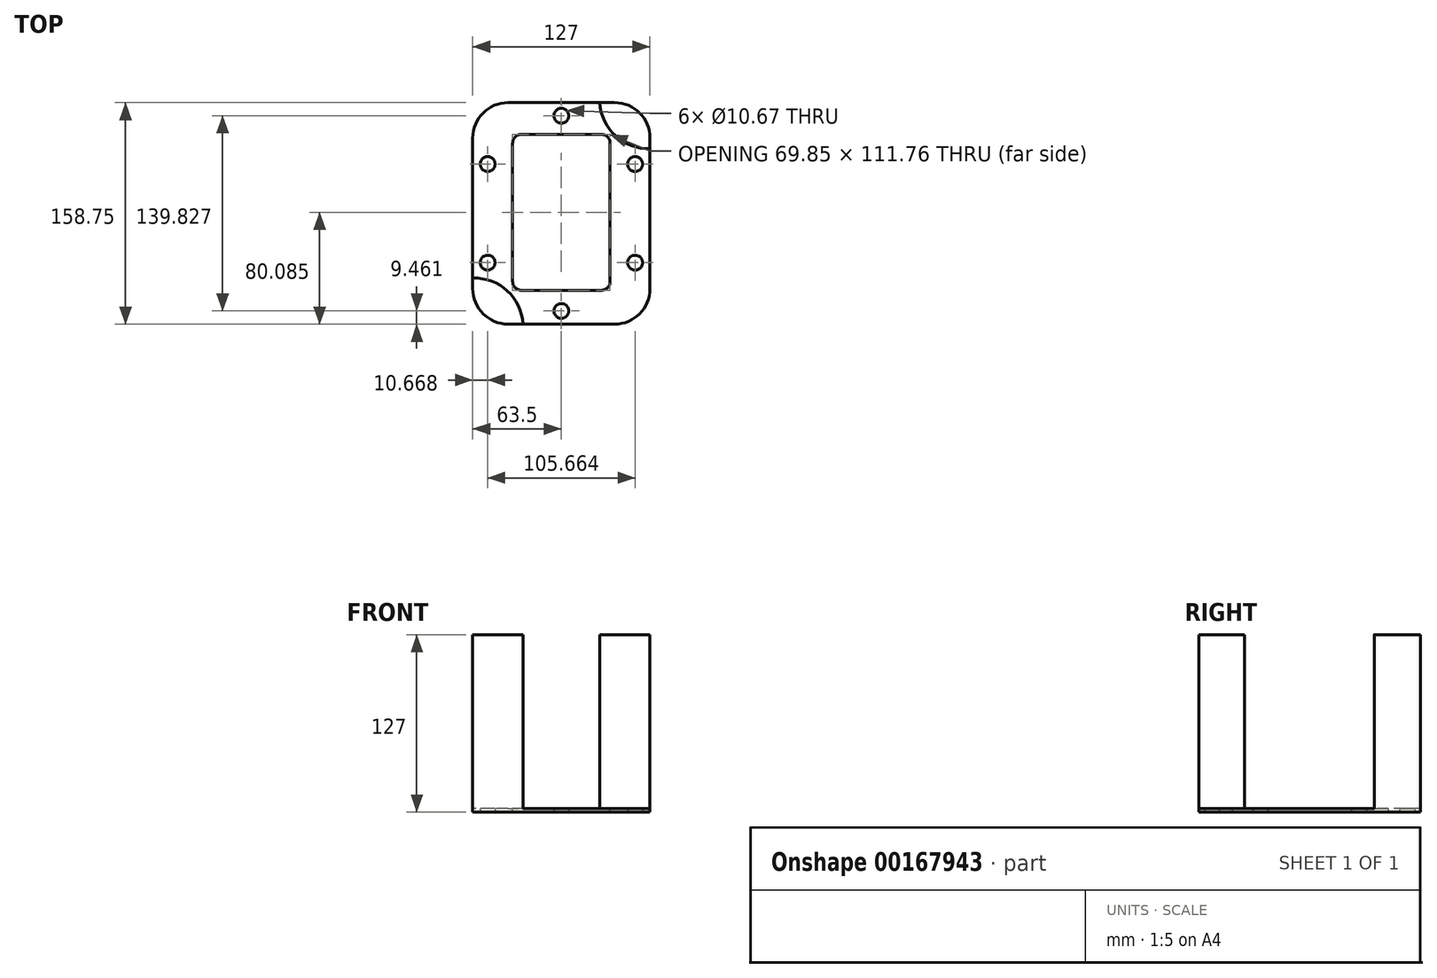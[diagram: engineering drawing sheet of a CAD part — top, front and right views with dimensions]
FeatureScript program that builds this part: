
annotation { "Feature Type Name" : "Feature", "Feature Type Description" : "" }
export const myFeature = defineFeature(function(context is Context, id is Id, definition is map)
    precondition{}
    {
        {
            var Q0;
            Q0=qCreatedBy(makeId("Top.planeOp"),FACE);
            var sketch = newSketch(context, id + "F0", { "sketchPlane" : qUnion([Q0])});
            skLineSegment(sketch, "E0.bottom", {"start": v(25.4, 0) * mm, "end": v(101.6, 0) * mm});
            skLineSegment(sketch, "E0.top", {"start": v(25.4, 158.75) * mm, "end": v(101.6, 158.75) * mm});
            skLineSegment(sketch, "E0.left", {"start": v(0, 25.4) * mm, "end": v(0, 133.35) * mm});
            skLineSegment(sketch, "E0.right", {"start": v(127, 25.4) * mm, "end": v(127, 133.35) * mm});
            skLineSegment(sketch, "E1", {"start": v(63.5, 0) * mm, "end": v(63.5, 158.75) * mm});
            skLineSegment(sketch, "E2", {"start": v(0, 79.38) * mm, "end": v(127, 79.38) * mm});
            skLineSegment(sketch, "E3", {"start": v(116.33, 79.38) * mm, "end": v(116.33, 114.68) * mm});
            skCircle(sketch, "E4", {"center": v(116.33, 114.68) * mm, "radius": 5.33 * mm});
            skCircle(sketch, "E5.MirrorC", {"center": v(10.67, 114.68) * mm, "radius": 5.33 * mm});
            skCircle(sketch, "E6.MirrorC", {"center": v(10.67, 44.07) * mm, "radius": 5.33 * mm});
            skCircle(sketch, "E7.MirrorC", {"center": v(116.33, 44.07) * mm, "radius": 5.33 * mm});
            skCircle(sketch, "E8", {"center": v(63.5, 149.29) * mm, "radius": 5.33 * mm});
            skCircle(sketch, "E9.MirrorC", {"center": v(63.5, 9.46) * mm, "radius": 5.33 * mm});
            skPoint(sketch, "E10.visualSharp", {"position": v(0, 158.75) * mm});
            skArc(sketch, "E10.filletArc", {"start": v(25.4, 158.75) * mm, "mid": v(7.44, 151.31) * mm, "end": v(0, 133.35) * mm});
            skPoint(sketch, "E11.visualSharp", {"position": v(0, 0) * mm});
            skArc(sketch, "E11.filletArc", {"start": v(0, 25.4) * mm, "mid": v(7.44, 7.44) * mm, "end": v(25.4, 0) * mm});
            skPoint(sketch, "E12.visualSharp", {"position": v(127, 0) * mm});
            skArc(sketch, "E12.filletArc", {"start": v(101.6, 0) * mm, "mid": v(119.56, 7.44) * mm, "end": v(127, 25.4) * mm});
            skPoint(sketch, "E13.visualSharp", {"position": v(127, 158.75) * mm});
            skArc(sketch, "E13.filletArc", {"start": v(127, 133.35) * mm, "mid": v(119.56, 151.31) * mm, "end": v(101.6, 158.75) * mm});
            skLineSegment(sketch, "E14.bottom", {"start": v(95.25, 135.26) * mm, "end": v(31.75, 135.26) * mm});
            skLineSegment(sketch, "E14.top", {"start": v(95.25, 23.5) * mm, "end": v(31.75, 23.5) * mm});
            skLineSegment(sketch, "E14.left", {"start": v(101.6, 128.9) * mm, "end": v(101.6, 29.84) * mm});
            skLineSegment(sketch, "E14.right", {"start": v(25.4, 128.9) * mm, "end": v(25.4, 29.84) * mm});
            skPoint(sketch, "E14.middle", {"position": v(63.5, 79.38) * mm});
            skPoint(sketch, "E15.visualSharp", {"position": v(25.4, 135.26) * mm});
            skArc(sketch, "E15.filletArc", {"start": v(31.75, 135.26) * mm, "mid": v(27.26, 133.4) * mm, "end": v(25.4, 128.9) * mm});
            skPoint(sketch, "E16.visualSharp", {"position": v(101.6, 135.26) * mm});
            skArc(sketch, "E16.filletArc", {"start": v(101.6, 128.9) * mm, "mid": v(99.74, 133.4) * mm, "end": v(95.25, 135.26) * mm});
            skPoint(sketch, "E17.visualSharp", {"position": v(101.6, 23.5) * mm});
            skArc(sketch, "E17.filletArc", {"start": v(95.25, 23.5) * mm, "mid": v(99.74, 25.35) * mm, "end": v(101.6, 29.84) * mm});
            skPoint(sketch, "E18.visualSharp", {"position": v(25.4, 23.5) * mm});
            skArc(sketch, "E18.filletArc", {"start": v(25.4, 29.84) * mm, "mid": v(27.26, 25.35) * mm, "end": v(31.75, 23.5) * mm});
            skSolve(sketch);
        }
        {
            var Q0;
            Q0 = qSketchRegion(id + "F0", true);
            var Q1;
            {var subQ0=sQuery(id+"F0.wireOp",EDGE,"E15.filletArc");Q1=makeQuery(id+"F0.imprint","IMPRINT",FACE,{"disambiguationData":[TD([[makeQuery(id+"F0.imprint","IMPRINT",EDGE,{"derivedFrom":subQ0}),1.0]])]});}
            var Q2;
            {var subQ0=sQuery(id+"F0.wireOp",EDGE,"E16.filletArc");Q2=makeQuery(id+"F0.imprint","IMPRINT",FACE,{"disambiguationData":[TD([[makeQuery(id+"F0.imprint","IMPRINT",EDGE,{"derivedFrom":subQ0}),1.0]])]});}
            var Q3;
            {var subQ0=sQuery(id+"F0.wireOp",EDGE,"E17.filletArc");Q3=makeQuery(id+"F0.imprint","IMPRINT",FACE,{"disambiguationData":[TD([[makeQuery(id+"F0.imprint","IMPRINT",EDGE,{"derivedFrom":subQ0}),1.0]])]});}
            var Q4;
            {var subQ0=sQuery(id+"F0.wireOp",EDGE,"E18.filletArc");Q4=makeQuery(id+"F0.imprint","IMPRINT",FACE,{"disambiguationData":[TD([[makeQuery(id+"F0.imprint","IMPRINT",EDGE,{"derivedFrom":subQ0}),1.0]])]});}
            extrude(context, id + "F1", {"entities" : qUnion([Q0, Q1, Q2, Q3, Q4]), "depth" : 127 * mm});
        }
        {
            var Q0;
            Q0=makeQuery(id+"F1.opExtrude","CAP_FACE",FACE,{"disambiguationData":[OSD([sQuery(id+"F0.wireOp",EDGE,"E0.bottom"),sQuery(id+"F0.wireOp",EDGE,"E0.top"),sQuery(id+"F0.wireOp",EDGE,"E0.left"),sQuery(id+"F0.wireOp",EDGE,"E0.right"),sQuery(id+"F0.wireOp",EDGE,"E4"),sQuery(id+"F0.wireOp",EDGE,"E5.MirrorC"),sQuery(id+"F0.wireOp",EDGE,"E6.MirrorC"),sQuery(id+"F0.wireOp",EDGE,"E7.MirrorC"),sQuery(id+"F0.wireOp",EDGE,"E8"),sQuery(id+"F0.wireOp",EDGE,"E9.MirrorC"),sQuery(id+"F0.wireOp",EDGE,"E10.filletArc"),sQuery(id+"F0.wireOp",EDGE,"E11.filletArc"),sQuery(id+"F0.wireOp",EDGE,"E12.filletArc"),sQuery(id+"F0.wireOp",EDGE,"E13.filletArc")])],"isStart":false});
            var sketch = newSketch(context, id + "F2", { "sketchPlane" : qUnion([Q0])});
            skLineSegment(sketch, "E19", {"start": v(63.5, 158.75) * mm, "end": v(63.5, 0) * mm, "construction": true});
            skLineSegment(sketch, "E20.0.1.1", {"start": v(0, 103.9) * mm, "end": v(25.4, 103.9) * mm});
            skLineSegment(sketch, "E20.0.1.4", {"start": v(127, 103.9) * mm, "end": v(101.6, 103.9) * mm});
            skLineSegment(sketch, "E20.0.1.5", {"start": v(127, 102.31) * mm, "end": v(101.6, 102.31) * mm});
            skLineSegment(sketch, "E20.0.1.6", {"start": v(101.6, 103.9) * mm, "end": v(101.6, 102.31) * mm});
            skLineSegment(sketch, "E20.0.1.7", {"start": v(127, 103.9) * mm, "end": v(101.6, 103.9) * mm});
            skLineSegment(sketch, "E20.0.2.0", {"start": v(0, 99.14) * mm, "end": v(25.4, 99.14) * mm});
            skLineSegment(sketch, "E20.0.2.1", {"start": v(0, 100.72) * mm, "end": v(25.4, 100.72) * mm});
            skLineSegment(sketch, "E20.0.2.2", {"start": v(0, 100.72) * mm, "end": v(25.4, 100.72) * mm});
            skLineSegment(sketch, "E20.0.2.3", {"start": v(25.4, 100.72) * mm, "end": v(25.4, 99.14) * mm});
            skLineSegment(sketch, "E20.0.2.4", {"start": v(127, 100.72) * mm, "end": v(101.6, 100.72) * mm});
            skLineSegment(sketch, "E20.0.2.5", {"start": v(127, 99.14) * mm, "end": v(101.6, 99.14) * mm});
            skLineSegment(sketch, "E20.0.2.6", {"start": v(101.6, 100.72) * mm, "end": v(101.6, 99.14) * mm});
            skLineSegment(sketch, "E20.0.2.7", {"start": v(127, 100.72) * mm, "end": v(101.6, 100.72) * mm});
            skLineSegment(sketch, "E20.0.3.0", {"start": v(0, 95.96) * mm, "end": v(25.4, 95.96) * mm});
            skLineSegment(sketch, "E20.0.3.1", {"start": v(0, 97.55) * mm, "end": v(25.4, 97.55) * mm});
            skLineSegment(sketch, "E20.0.3.2", {"start": v(0, 97.55) * mm, "end": v(25.4, 97.55) * mm});
            skLineSegment(sketch, "E20.0.3.3", {"start": v(25.4, 97.55) * mm, "end": v(25.4, 95.96) * mm});
            skLineSegment(sketch, "E20.0.3.4", {"start": v(127, 97.55) * mm, "end": v(101.6, 97.55) * mm});
            skLineSegment(sketch, "E20.0.3.5", {"start": v(127, 95.96) * mm, "end": v(101.6, 95.96) * mm});
            skLineSegment(sketch, "E20.0.3.6", {"start": v(101.6, 97.55) * mm, "end": v(101.6, 95.96) * mm});
            skLineSegment(sketch, "E20.0.3.7", {"start": v(127, 97.55) * mm, "end": v(101.6, 97.55) * mm});
            skLineSegment(sketch, "E20.0.4.0", {"start": v(0, 92.79) * mm, "end": v(25.4, 92.79) * mm});
            skLineSegment(sketch, "E20.0.4.1", {"start": v(0, 94.37) * mm, "end": v(25.4, 94.37) * mm});
            skLineSegment(sketch, "E20.0.4.2", {"start": v(0, 94.37) * mm, "end": v(25.4, 94.37) * mm});
            skLineSegment(sketch, "E20.0.4.3", {"start": v(25.4, 94.37) * mm, "end": v(25.4, 92.79) * mm});
            skLineSegment(sketch, "E20.0.4.4", {"start": v(127, 94.37) * mm, "end": v(101.6, 94.37) * mm});
            skLineSegment(sketch, "E20.0.4.5", {"start": v(127, 92.79) * mm, "end": v(101.6, 92.79) * mm});
            skLineSegment(sketch, "E20.0.4.6", {"start": v(101.6, 94.37) * mm, "end": v(101.6, 92.79) * mm});
            skLineSegment(sketch, "E20.0.4.7", {"start": v(127, 94.37) * mm, "end": v(101.6, 94.37) * mm});
            skLineSegment(sketch, "E20.0.5.0", {"start": v(0, 89.61) * mm, "end": v(25.4, 89.61) * mm});
            skLineSegment(sketch, "E20.0.5.1", {"start": v(0, 91.2) * mm, "end": v(25.4, 91.2) * mm});
            skLineSegment(sketch, "E20.0.5.2", {"start": v(0, 91.2) * mm, "end": v(25.4, 91.2) * mm});
            skLineSegment(sketch, "E20.0.5.3", {"start": v(25.4, 91.2) * mm, "end": v(25.4, 89.61) * mm});
            skLineSegment(sketch, "E20.0.5.4", {"start": v(127, 91.2) * mm, "end": v(101.6, 91.2) * mm});
            skLineSegment(sketch, "E20.0.5.5", {"start": v(127, 89.61) * mm, "end": v(101.6, 89.61) * mm});
            skLineSegment(sketch, "E20.0.5.6", {"start": v(101.6, 91.2) * mm, "end": v(101.6, 89.61) * mm});
            skLineSegment(sketch, "E20.0.5.7", {"start": v(127, 91.2) * mm, "end": v(101.6, 91.2) * mm});
            skLineSegment(sketch, "E20.0.6.0", {"start": v(0, 86.44) * mm, "end": v(25.4, 86.44) * mm});
            skLineSegment(sketch, "E20.0.6.1", {"start": v(0, 88.02) * mm, "end": v(25.4, 88.02) * mm});
            skLineSegment(sketch, "E20.0.6.2", {"start": v(0, 88.02) * mm, "end": v(25.4, 88.02) * mm});
            skLineSegment(sketch, "E20.0.6.3", {"start": v(25.4, 88.02) * mm, "end": v(25.4, 86.44) * mm});
            skLineSegment(sketch, "E20.0.6.4", {"start": v(127, 88.02) * mm, "end": v(101.6, 88.02) * mm});
            skLineSegment(sketch, "E20.0.6.5", {"start": v(127, 86.44) * mm, "end": v(101.6, 86.44) * mm});
            skLineSegment(sketch, "E20.0.6.6", {"start": v(101.6, 88.02) * mm, "end": v(101.6, 86.44) * mm});
            skLineSegment(sketch, "E20.0.6.7", {"start": v(127, 88.02) * mm, "end": v(101.6, 88.02) * mm});
            skLineSegment(sketch, "E20.0.7.0", {"start": v(0, 83.26) * mm, "end": v(25.4, 83.26) * mm});
            skLineSegment(sketch, "E20.0.7.1", {"start": v(0, 84.85) * mm, "end": v(25.4, 84.85) * mm});
            skLineSegment(sketch, "E20.0.7.2", {"start": v(0, 84.85) * mm, "end": v(25.4, 84.85) * mm});
            skLineSegment(sketch, "E20.0.7.3", {"start": v(25.4, 84.85) * mm, "end": v(25.4, 83.26) * mm});
            skLineSegment(sketch, "E20.0.7.4", {"start": v(127, 84.85) * mm, "end": v(101.6, 84.85) * mm});
            skLineSegment(sketch, "E20.0.7.5", {"start": v(127, 83.26) * mm, "end": v(101.6, 83.26) * mm});
            skLineSegment(sketch, "E20.0.7.6", {"start": v(101.6, 84.85) * mm, "end": v(101.6, 83.26) * mm});
            skLineSegment(sketch, "E20.0.7.7", {"start": v(127, 84.85) * mm, "end": v(101.6, 84.85) * mm});
            skLineSegment(sketch, "E20.0.8.0", {"start": v(0, 80.09) * mm, "end": v(25.4, 80.09) * mm});
            skLineSegment(sketch, "E20.0.8.1", {"start": v(0, 81.67) * mm, "end": v(25.4, 81.67) * mm});
            skLineSegment(sketch, "E20.0.8.2", {"start": v(0, 81.67) * mm, "end": v(25.4, 81.67) * mm});
            skLineSegment(sketch, "E20.0.8.3", {"start": v(25.4, 81.67) * mm, "end": v(25.4, 80.09) * mm});
            skLineSegment(sketch, "E20.0.8.4", {"start": v(127, 81.67) * mm, "end": v(101.6, 81.67) * mm});
            skLineSegment(sketch, "E20.0.8.5", {"start": v(127, 80.09) * mm, "end": v(101.6, 80.09) * mm});
            skLineSegment(sketch, "E20.0.8.6", {"start": v(101.6, 81.67) * mm, "end": v(101.6, 80.09) * mm});
            skLineSegment(sketch, "E20.0.8.7", {"start": v(127, 81.67) * mm, "end": v(101.6, 81.67) * mm});
            skLineSegment(sketch, "E20.0.9.0", {"start": v(0, 76.91) * mm, "end": v(25.4, 76.91) * mm});
            skLineSegment(sketch, "E20.0.9.1", {"start": v(0, 78.5) * mm, "end": v(25.4, 78.5) * mm});
            skLineSegment(sketch, "E20.0.9.2", {"start": v(0, 78.5) * mm, "end": v(25.4, 78.5) * mm});
            skLineSegment(sketch, "E20.0.9.3", {"start": v(25.4, 78.5) * mm, "end": v(25.4, 76.91) * mm});
            skLineSegment(sketch, "E20.0.9.4", {"start": v(127, 78.5) * mm, "end": v(101.6, 78.5) * mm});
            skLineSegment(sketch, "E20.0.9.5", {"start": v(127, 76.91) * mm, "end": v(101.6, 76.91) * mm});
            skLineSegment(sketch, "E20.0.9.6", {"start": v(101.6, 78.5) * mm, "end": v(101.6, 76.91) * mm});
            skLineSegment(sketch, "E20.0.9.7", {"start": v(127, 78.5) * mm, "end": v(101.6, 78.5) * mm});
            skLineSegment(sketch, "E20.0.10.0", {"start": v(0, 73.74) * mm, "end": v(25.4, 73.74) * mm});
            skLineSegment(sketch, "E20.0.10.1", {"start": v(0, 75.32) * mm, "end": v(25.4, 75.32) * mm});
            skLineSegment(sketch, "E20.0.10.2", {"start": v(0, 75.32) * mm, "end": v(25.4, 75.32) * mm});
            skLineSegment(sketch, "E20.0.10.3", {"start": v(25.4, 75.32) * mm, "end": v(25.4, 73.74) * mm});
            skLineSegment(sketch, "E20.0.10.4", {"start": v(127, 75.32) * mm, "end": v(101.6, 75.32) * mm});
            skLineSegment(sketch, "E20.0.10.5", {"start": v(127, 73.74) * mm, "end": v(101.6, 73.74) * mm});
            skLineSegment(sketch, "E20.0.10.6", {"start": v(101.6, 75.32) * mm, "end": v(101.6, 73.74) * mm});
            skLineSegment(sketch, "E20.0.10.7", {"start": v(127, 75.32) * mm, "end": v(101.6, 75.32) * mm});
            skLineSegment(sketch, "E20.0.11.0", {"start": v(0, 70.56) * mm, "end": v(25.4, 70.56) * mm});
            skLineSegment(sketch, "E20.0.11.1", {"start": v(0, 72.15) * mm, "end": v(25.4, 72.15) * mm});
            skLineSegment(sketch, "E20.0.11.2", {"start": v(0, 72.15) * mm, "end": v(25.4, 72.15) * mm});
            skLineSegment(sketch, "E20.0.11.3", {"start": v(25.4, 72.15) * mm, "end": v(25.4, 70.56) * mm});
            skLineSegment(sketch, "E20.0.11.4", {"start": v(127, 72.15) * mm, "end": v(101.6, 72.15) * mm});
            skLineSegment(sketch, "E20.0.11.5", {"start": v(127, 70.56) * mm, "end": v(101.6, 70.56) * mm});
            skLineSegment(sketch, "E20.0.11.6", {"start": v(101.6, 72.15) * mm, "end": v(101.6, 70.56) * mm});
            skLineSegment(sketch, "E20.0.11.7", {"start": v(127, 72.15) * mm, "end": v(101.6, 72.15) * mm});
            skLineSegment(sketch, "E20.0.12.0", {"start": v(0, 67.39) * mm, "end": v(25.4, 67.39) * mm});
            skLineSegment(sketch, "E20.0.12.1", {"start": v(0, 68.97) * mm, "end": v(25.4, 68.97) * mm});
            skLineSegment(sketch, "E20.0.12.2", {"start": v(0, 68.97) * mm, "end": v(25.4, 68.97) * mm});
            skLineSegment(sketch, "E20.0.12.3", {"start": v(25.4, 68.97) * mm, "end": v(25.4, 67.39) * mm});
            skLineSegment(sketch, "E20.0.12.4", {"start": v(127, 68.97) * mm, "end": v(101.6, 68.97) * mm});
            skLineSegment(sketch, "E20.0.12.5", {"start": v(127, 67.39) * mm, "end": v(101.6, 67.39) * mm});
            skLineSegment(sketch, "E20.0.12.6", {"start": v(101.6, 68.97) * mm, "end": v(101.6, 67.39) * mm});
            skLineSegment(sketch, "E20.0.12.7", {"start": v(127, 68.97) * mm, "end": v(101.6, 68.97) * mm});
            skLineSegment(sketch, "E20.0.13.0", {"start": v(0, 64.21) * mm, "end": v(25.4, 64.21) * mm});
            skLineSegment(sketch, "E20.0.13.1", {"start": v(0, 65.8) * mm, "end": v(25.4, 65.8) * mm});
            skLineSegment(sketch, "E20.0.13.2", {"start": v(0, 65.8) * mm, "end": v(25.4, 65.8) * mm});
            skLineSegment(sketch, "E20.0.13.3", {"start": v(25.4, 65.8) * mm, "end": v(25.4, 64.21) * mm});
            skLineSegment(sketch, "E20.0.13.4", {"start": v(127, 65.8) * mm, "end": v(101.6, 65.8) * mm});
            skLineSegment(sketch, "E20.0.13.5", {"start": v(127, 64.21) * mm, "end": v(101.6, 64.21) * mm});
            skLineSegment(sketch, "E20.0.13.6", {"start": v(101.6, 65.8) * mm, "end": v(101.6, 64.21) * mm});
            skLineSegment(sketch, "E20.0.13.7", {"start": v(127, 65.8) * mm, "end": v(101.6, 65.8) * mm});
            skLineSegment(sketch, "E20.0.14.0", {"start": v(0, 61.04) * mm, "end": v(25.4, 61.04) * mm});
            skLineSegment(sketch, "E20.0.14.1", {"start": v(0, 62.62) * mm, "end": v(25.4, 62.62) * mm});
            skLineSegment(sketch, "E20.0.14.2", {"start": v(0, 62.62) * mm, "end": v(25.4, 62.62) * mm});
            skLineSegment(sketch, "E20.0.14.3", {"start": v(25.4, 62.62) * mm, "end": v(25.4, 61.04) * mm});
            skLineSegment(sketch, "E20.0.14.4", {"start": v(127, 62.62) * mm, "end": v(101.6, 62.62) * mm});
            skLineSegment(sketch, "E20.0.14.5", {"start": v(127, 61.04) * mm, "end": v(101.6, 61.04) * mm});
            skLineSegment(sketch, "E20.0.14.6", {"start": v(101.6, 62.62) * mm, "end": v(101.6, 61.04) * mm});
            skLineSegment(sketch, "E20.0.14.7", {"start": v(127, 62.62) * mm, "end": v(101.6, 62.62) * mm});
            skLineSegment(sketch, "E20.0.15.0", {"start": v(0, 57.86) * mm, "end": v(25.4, 57.86) * mm});
            skLineSegment(sketch, "E20.0.15.1", {"start": v(0, 59.45) * mm, "end": v(25.4, 59.45) * mm});
            skLineSegment(sketch, "E20.0.15.2", {"start": v(0, 59.45) * mm, "end": v(25.4, 59.45) * mm});
            skLineSegment(sketch, "E20.0.15.3", {"start": v(25.4, 59.45) * mm, "end": v(25.4, 57.86) * mm});
            skLineSegment(sketch, "E20.0.15.4", {"start": v(127, 59.45) * mm, "end": v(101.6, 59.45) * mm});
            skLineSegment(sketch, "E20.0.15.5", {"start": v(127, 57.86) * mm, "end": v(101.6, 57.86) * mm});
            skLineSegment(sketch, "E20.0.15.6", {"start": v(101.6, 59.45) * mm, "end": v(101.6, 57.86) * mm});
            skLineSegment(sketch, "E20.0.15.7", {"start": v(127, 59.45) * mm, "end": v(101.6, 59.45) * mm});
            skLineSegment(sketch, "E20.0.16.0", {"start": v(0, 54.69) * mm, "end": v(25.4, 54.69) * mm});
            skLineSegment(sketch, "E20.0.16.1", {"start": v(0, 56.27) * mm, "end": v(25.4, 56.27) * mm});
            skLineSegment(sketch, "E20.0.16.2", {"start": v(0, 56.27) * mm, "end": v(25.4, 56.27) * mm});
            skLineSegment(sketch, "E20.0.16.3", {"start": v(25.4, 56.27) * mm, "end": v(25.4, 54.69) * mm});
            skLineSegment(sketch, "E20.0.16.4", {"start": v(127, 56.27) * mm, "end": v(101.6, 56.27) * mm});
            skLineSegment(sketch, "E20.0.16.5", {"start": v(127, 54.69) * mm, "end": v(101.6, 54.69) * mm});
            skLineSegment(sketch, "E20.0.16.6", {"start": v(101.6, 56.27) * mm, "end": v(101.6, 54.69) * mm});
            skLineSegment(sketch, "E20.0.16.7", {"start": v(127, 56.27) * mm, "end": v(101.6, 56.27) * mm});
            skLineSegment(sketch, "E21", {"start": v(0, 105.16) * mm, "end": v(10.16, 105.16) * mm});
            skLineSegment(sketch, "E22", {"start": v(0, 124.2) * mm, "end": v(10.16, 124.2) * mm});
            skArc(sketch, "E23", {"start": v(10.16, 105.16) * mm, "mid": v(19.69, 114.68) * mm, "end": v(10.16, 124.2) * mm});
            skLineSegment(sketch, "E24.MirrorCS", {"start": v(127, 124.2) * mm, "end": v(116.84, 124.2) * mm});
            skArc(sketch, "E25.MirrorCS", {"start": v(116.84, 105.16) * mm, "mid": v(107.31, 114.68) * mm, "end": v(116.84, 124.2) * mm});
            skLineSegment(sketch, "E26.MirrorCS", {"start": v(127, 105.16) * mm, "end": v(116.84, 105.16) * mm});
            skLineSegment(sketch, "E27", {"start": v(63.5, 79.38) * mm, "end": v(90.41, 79.38) * mm});
            skLineSegment(sketch, "E28.MirrorCS", {"start": v(0, 34.54) * mm, "end": v(10.16, 34.54) * mm});
            skArc(sketch, "E29.MirrorCS", {"start": v(10.16, 53.6) * mm, "mid": v(19.69, 44.07) * mm, "end": v(10.16, 34.54) * mm});
            skLineSegment(sketch, "E30.MirrorCS", {"start": v(0, 53.6) * mm, "end": v(10.16, 53.6) * mm});
            skArc(sketch, "E31.MirrorCS", {"start": v(116.84, 53.6) * mm, "mid": v(107.31, 44.07) * mm, "end": v(116.84, 34.54) * mm});
            skLineSegment(sketch, "E32.MirrorCS", {"start": v(127, 34.54) * mm, "end": v(116.84, 34.54) * mm});
            skLineSegment(sketch, "E33.MirrorCS", {"start": v(127, 53.6) * mm, "end": v(116.84, 53.6) * mm});
            skLineSegment(sketch, "E34", {"start": v(25.4, 103.9) * mm, "end": v(25.4, 102.32) * mm});
            skLineSegment(sketch, "E35", {"start": v(25.4, 102.32) * mm, "end": v(0, 102.32) * mm});
            skSolve(sketch);
        }
        {
            var Q0;
            {var subQ1=sQuery(id+"F2.wireOp",EDGE,"E21");Q0=makeQuery(id+"F2.imprint","IMPRINT",FACE,{"disambiguationData":[TD([[makeQuery(id+"F2.imprint","IMPRINT",EDGE,{"derivedFrom":subQ1}),1.0]])]});}
            var Q1;
            {var subQ0=sQuery(id+"F2.wireOp",EDGE,"E20.0.1.1");Q1=makeQuery(id+"F2.imprint","IMPRINT",FACE,{"disambiguationData":[TD([[makeQuery(id+"F2.imprint","IMPRINT",EDGE,{"derivedFrom":subQ0}),-1.0]])]});}
            var Q2;
            {var subQ0=sQuery(id+"F2.wireOp",EDGE,"E20.0.2.0");Q2=makeQuery(id+"F2.imprint","IMPRINT",FACE,{"disambiguationData":[TD([[makeQuery(id+"F2.imprint","IMPRINT",EDGE,{"derivedFrom":subQ0}),1.0]])]});}
            var Q3;
            {var subQ0=sQuery(id+"F2.wireOp",EDGE,"E20.0.3.0");Q3=makeQuery(id+"F2.imprint","IMPRINT",FACE,{"disambiguationData":[TD([[makeQuery(id+"F2.imprint","IMPRINT",EDGE,{"derivedFrom":subQ0}),1.0]])]});}
            var Q4;
            {var subQ0=sQuery(id+"F2.wireOp",EDGE,"E20.0.4.0");Q4=makeQuery(id+"F2.imprint","IMPRINT",FACE,{"disambiguationData":[TD([[makeQuery(id+"F2.imprint","IMPRINT",EDGE,{"derivedFrom":subQ0}),1.0]])]});}
            var Q5;
            {var subQ0=sQuery(id+"F2.wireOp",EDGE,"E20.0.5.0");Q5=makeQuery(id+"F2.imprint","IMPRINT",FACE,{"disambiguationData":[TD([[makeQuery(id+"F2.imprint","IMPRINT",EDGE,{"derivedFrom":subQ0}),1.0]])]});}
            var Q6;
            {var subQ0=sQuery(id+"F2.wireOp",EDGE,"E20.0.6.0");Q6=makeQuery(id+"F2.imprint","IMPRINT",FACE,{"disambiguationData":[TD([[makeQuery(id+"F2.imprint","IMPRINT",EDGE,{"derivedFrom":subQ0}),1.0]])]});}
            var Q7;
            {var subQ0=sQuery(id+"F2.wireOp",EDGE,"E20.0.7.0");Q7=makeQuery(id+"F2.imprint","IMPRINT",FACE,{"disambiguationData":[TD([[makeQuery(id+"F2.imprint","IMPRINT",EDGE,{"derivedFrom":subQ0}),1.0]])]});}
            var Q8;
            {var subQ0=sQuery(id+"F2.wireOp",EDGE,"E20.0.8.0");Q8=makeQuery(id+"F2.imprint","IMPRINT",FACE,{"disambiguationData":[TD([[makeQuery(id+"F2.imprint","IMPRINT",EDGE,{"derivedFrom":subQ0}),1.0]])]});}
            var Q9;
            {var subQ0=sQuery(id+"F2.wireOp",EDGE,"E20.0.9.0");Q9=makeQuery(id+"F2.imprint","IMPRINT",FACE,{"disambiguationData":[TD([[makeQuery(id+"F2.imprint","IMPRINT",EDGE,{"derivedFrom":subQ0}),1.0]])]});}
            var Q10;
            {var subQ0=sQuery(id+"F2.wireOp",EDGE,"E20.0.10.0");Q10=makeQuery(id+"F2.imprint","IMPRINT",FACE,{"disambiguationData":[TD([[makeQuery(id+"F2.imprint","IMPRINT",EDGE,{"derivedFrom":subQ0}),1.0]])]});}
            var Q11;
            {var subQ0=sQuery(id+"F2.wireOp",EDGE,"E20.0.11.0");Q11=makeQuery(id+"F2.imprint","IMPRINT",FACE,{"disambiguationData":[TD([[makeQuery(id+"F2.imprint","IMPRINT",EDGE,{"derivedFrom":subQ0}),1.0]])]});}
            var Q12;
            {var subQ0=sQuery(id+"F2.wireOp",EDGE,"E20.0.12.0");Q12=makeQuery(id+"F2.imprint","IMPRINT",FACE,{"disambiguationData":[TD([[makeQuery(id+"F2.imprint","IMPRINT",EDGE,{"derivedFrom":subQ0}),1.0]])]});}
            var Q13;
            {var subQ0=sQuery(id+"F2.wireOp",EDGE,"E20.0.13.0");Q13=makeQuery(id+"F2.imprint","IMPRINT",FACE,{"disambiguationData":[TD([[makeQuery(id+"F2.imprint","IMPRINT",EDGE,{"derivedFrom":subQ0}),1.0]])]});}
            var Q14;
            {var subQ0=sQuery(id+"F2.wireOp",EDGE,"E20.0.14.0");Q14=makeQuery(id+"F2.imprint","IMPRINT",FACE,{"disambiguationData":[TD([[makeQuery(id+"F2.imprint","IMPRINT",EDGE,{"derivedFrom":subQ0}),1.0]])]});}
            var Q15;
            {var subQ0=sQuery(id+"F2.wireOp",EDGE,"E20.0.15.0");Q15=makeQuery(id+"F2.imprint","IMPRINT",FACE,{"disambiguationData":[TD([[makeQuery(id+"F2.imprint","IMPRINT",EDGE,{"derivedFrom":subQ0}),1.0]])]});}
            var Q16;
            {var subQ0=sQuery(id+"F2.wireOp",EDGE,"E28.MirrorCS");Q16=makeQuery(id+"F2.imprint","IMPRINT",FACE,{"disambiguationData":[TD([[makeQuery(id+"F2.imprint","IMPRINT",EDGE,{"derivedFrom":subQ0}),1.0]])]});}
            var Q17;
            {var subQ0=sQuery(id+"F2.wireOp",EDGE,"E20.0.16.0");Q17=makeQuery(id+"F2.imprint","IMPRINT",FACE,{"disambiguationData":[TD([[makeQuery(id+"F2.imprint","IMPRINT",EDGE,{"derivedFrom":subQ0}),1.0]])]});}
            var Q18;
            Q18=makeQuery(id+"F2.imprint","IMPRINT",FACE,{"disambiguationData":[TD([[makeQuery(id+"F2.imprint","IMPRINT",EDGE,{"derivedFrom":sQuery(id+"F2.wireOp",EDGE,"E31.MirrorCS")}),1.0]])]});
            var Q19;
            {var subQ0=sQuery(id+"F2.wireOp",EDGE,"E20.0.16.5");Q19=makeQuery(id+"F2.imprint","IMPRINT",FACE,{"disambiguationData":[TD([[makeQuery(id+"F2.imprint","IMPRINT",EDGE,{"derivedFrom":subQ0}),-1.0]])]});}
            var Q20;
            {var subQ0=sQuery(id+"F2.wireOp",EDGE,"E20.0.15.5");Q20=makeQuery(id+"F2.imprint","IMPRINT",FACE,{"disambiguationData":[TD([[makeQuery(id+"F2.imprint","IMPRINT",EDGE,{"derivedFrom":subQ0}),-1.0]])]});}
            var Q21;
            {var subQ0=sQuery(id+"F2.wireOp",EDGE,"E20.0.14.5");Q21=makeQuery(id+"F2.imprint","IMPRINT",FACE,{"disambiguationData":[TD([[makeQuery(id+"F2.imprint","IMPRINT",EDGE,{"derivedFrom":subQ0}),-1.0]])]});}
            var Q22;
            {var subQ0=sQuery(id+"F2.wireOp",EDGE,"E20.0.13.5");Q22=makeQuery(id+"F2.imprint","IMPRINT",FACE,{"disambiguationData":[TD([[makeQuery(id+"F2.imprint","IMPRINT",EDGE,{"derivedFrom":subQ0}),-1.0]])]});}
            var Q23;
            {var subQ0=sQuery(id+"F2.wireOp",EDGE,"E20.0.12.5");Q23=makeQuery(id+"F2.imprint","IMPRINT",FACE,{"disambiguationData":[TD([[makeQuery(id+"F2.imprint","IMPRINT",EDGE,{"derivedFrom":subQ0}),-1.0]])]});}
            var Q24;
            {var subQ0=sQuery(id+"F2.wireOp",EDGE,"E20.0.11.5");Q24=makeQuery(id+"F2.imprint","IMPRINT",FACE,{"disambiguationData":[TD([[makeQuery(id+"F2.imprint","IMPRINT",EDGE,{"derivedFrom":subQ0}),-1.0]])]});}
            var Q25;
            {var subQ0=sQuery(id+"F2.wireOp",EDGE,"E20.0.10.5");Q25=makeQuery(id+"F2.imprint","IMPRINT",FACE,{"disambiguationData":[TD([[makeQuery(id+"F2.imprint","IMPRINT",EDGE,{"derivedFrom":subQ0}),-1.0]])]});}
            var Q26;
            {var subQ0=sQuery(id+"F2.wireOp",EDGE,"E20.0.9.5");Q26=makeQuery(id+"F2.imprint","IMPRINT",FACE,{"disambiguationData":[TD([[makeQuery(id+"F2.imprint","IMPRINT",EDGE,{"derivedFrom":subQ0}),-1.0]])]});}
            var Q27;
            {var subQ0=sQuery(id+"F2.wireOp",EDGE,"E20.0.8.5");Q27=makeQuery(id+"F2.imprint","IMPRINT",FACE,{"disambiguationData":[TD([[makeQuery(id+"F2.imprint","IMPRINT",EDGE,{"derivedFrom":subQ0}),-1.0]])]});}
            var Q28;
            {var subQ0=sQuery(id+"F2.wireOp",EDGE,"E20.0.7.5");Q28=makeQuery(id+"F2.imprint","IMPRINT",FACE,{"disambiguationData":[TD([[makeQuery(id+"F2.imprint","IMPRINT",EDGE,{"derivedFrom":subQ0}),-1.0]])]});}
            var Q29;
            {var subQ0=sQuery(id+"F2.wireOp",EDGE,"E20.0.6.5");Q29=makeQuery(id+"F2.imprint","IMPRINT",FACE,{"disambiguationData":[TD([[makeQuery(id+"F2.imprint","IMPRINT",EDGE,{"derivedFrom":subQ0}),-1.0]])]});}
            var Q30;
            {var subQ0=sQuery(id+"F2.wireOp",EDGE,"E20.0.5.5");Q30=makeQuery(id+"F2.imprint","IMPRINT",FACE,{"disambiguationData":[TD([[makeQuery(id+"F2.imprint","IMPRINT",EDGE,{"derivedFrom":subQ0}),-1.0]])]});}
            var Q31;
            {var subQ0=sQuery(id+"F2.wireOp",EDGE,"E20.0.4.5");Q31=makeQuery(id+"F2.imprint","IMPRINT",FACE,{"disambiguationData":[TD([[makeQuery(id+"F2.imprint","IMPRINT",EDGE,{"derivedFrom":subQ0}),-1.0]])]});}
            var Q32;
            {var subQ0=sQuery(id+"F2.wireOp",EDGE,"E20.0.3.5");Q32=makeQuery(id+"F2.imprint","IMPRINT",FACE,{"disambiguationData":[TD([[makeQuery(id+"F2.imprint","IMPRINT",EDGE,{"derivedFrom":subQ0}),-1.0]])]});}
            var Q33;
            {var subQ0=sQuery(id+"F2.wireOp",EDGE,"E20.0.2.5");Q33=makeQuery(id+"F2.imprint","IMPRINT",FACE,{"disambiguationData":[TD([[makeQuery(id+"F2.imprint","IMPRINT",EDGE,{"derivedFrom":subQ0}),-1.0]])]});}
            var Q34;
            {var subQ0=sQuery(id+"F2.wireOp",EDGE,"E20.0.1.5");Q34=makeQuery(id+"F2.imprint","IMPRINT",FACE,{"disambiguationData":[TD([[makeQuery(id+"F2.imprint","IMPRINT",EDGE,{"derivedFrom":subQ0}),-1.0]])]});}
            var Q35;
            {var subQ1=sQuery(id+"F2.wireOp",EDGE,"E24.MirrorCS");Q35=makeQuery(id+"F2.imprint","IMPRINT",FACE,{"disambiguationData":[TD([[makeQuery(id+"F2.imprint","IMPRINT",EDGE,{"derivedFrom":subQ1}),1.0]])]});}
            var Q36;
            {var subQ0=sQuery(id+"F2.wireOp",EDGE,"E20.0.4.5");Q36=makeQuery(id+"F2.imprint","IMPRINT",FACE,{"disambiguationData":[TD([[makeQuery(id+"F2.imprint","IMPRINT",EDGE,{"derivedFrom":subQ0}),-1.0]])]});}
            var Q37;
            {var subQ0=sQuery(id+"F2.wireOp",EDGE,"E20.0.3.5");Q37=makeQuery(id+"F2.imprint","IMPRINT",FACE,{"disambiguationData":[TD([[makeQuery(id+"F2.imprint","IMPRINT",EDGE,{"derivedFrom":subQ0}),-1.0]])]});}
            var Q38;
            {var subQ0=sQuery(id+"F2.wireOp",EDGE,"E20.0.2.5");Q38=makeQuery(id+"F2.imprint","IMPRINT",FACE,{"disambiguationData":[TD([[makeQuery(id+"F2.imprint","IMPRINT",EDGE,{"derivedFrom":subQ0}),-1.0]])]});}
            var Q39;
            {var subQ1=sQuery(id+"F2.wireOp",EDGE,"E24.MirrorCS");Q39=makeQuery(id+"F2.imprint","IMPRINT",FACE,{"disambiguationData":[TD([[makeQuery(id+"F2.imprint","IMPRINT",EDGE,{"derivedFrom":subQ1}),1.0]])]});}
            var Q40;
            {var subQ0=sQuery(id+"F2.wireOp",EDGE,"E20.0.1.5");Q40=makeQuery(id+"F2.imprint","IMPRINT",FACE,{"disambiguationData":[TD([[makeQuery(id+"F2.imprint","IMPRINT",EDGE,{"derivedFrom":subQ0}),-1.0]])]});}
            extrude(context, id + "F3", {"entities" : qUnion([Q0, Q1, Q2, Q3, Q4, Q5, Q6, Q7, Q8, Q9, Q10, Q11, Q12, Q13, Q14, Q15, Q16, Q17, Q18, Q19, Q20, Q21, Q22, Q23, Q24, Q25, Q26, Q27, Q28, Q29, Q30, Q31, Q32, Q33, Q34, Q35, Q36, Q37, Q38, Q39, Q40]), "operationType" : NewBodyOperationType.REMOVE, "oppositeDirection" : true, "depth" : 124.46 * mm});
        }
        {
            var Q0;
            Q0=makeQuery(id+"F1.opExtrude","CAP_FACE",FACE,{"disambiguationData":[OSD([sQuery(id+"F0.wireOp",EDGE,"E0.bottom"),sQuery(id+"F0.wireOp",EDGE,"E0.top"),sQuery(id+"F0.wireOp",EDGE,"E0.left"),sQuery(id+"F0.wireOp",EDGE,"E0.right"),sQuery(id+"F0.wireOp",EDGE,"E4"),sQuery(id+"F0.wireOp",EDGE,"E5.MirrorC"),sQuery(id+"F0.wireOp",EDGE,"E6.MirrorC"),sQuery(id+"F0.wireOp",EDGE,"E7.MirrorC"),sQuery(id+"F0.wireOp",EDGE,"E8"),sQuery(id+"F0.wireOp",EDGE,"E9.MirrorC"),sQuery(id+"F0.wireOp",EDGE,"E10.filletArc"),sQuery(id+"F0.wireOp",EDGE,"E11.filletArc"),sQuery(id+"F0.wireOp",EDGE,"E12.filletArc"),sQuery(id+"F0.wireOp",EDGE,"E13.filletArc")])],"isStart":false});
            var sketch = newSketch(context, id + "F4", { "sketchPlane" : qUnion([Q0])});
            skLineSegment(sketch, "E36", {"start": v(63.5, 158.75) * mm, "end": v(63.5, 0) * mm});
            skLineSegment(sketch, "E37", {"start": v(63.5, 80.09) * mm, "end": v(93.16, 80.09) * mm});
            skPoint(sketch, "E37.startSnap0", {"position": v(12.7, 80.09) * mm});
            skLineSegment(sketch, "E38.bottom", {"start": v(92.08, 135.97) * mm, "end": v(34.93, 135.97) * mm});
            skLineSegment(sketch, "E38.top", {"start": v(92.08, 24.2) * mm, "end": v(34.93, 24.2) * mm});
            skLineSegment(sketch, "E38.left", {"start": v(98.43, 129.62) * mm, "end": v(98.43, 30.56) * mm});
            skLineSegment(sketch, "E38.right", {"start": v(28.58, 129.62) * mm, "end": v(28.58, 30.56) * mm});
            skPoint(sketch, "E38.middle", {"position": v(63.5, 80.09) * mm});
            skPoint(sketch, "E39.visualSharp", {"position": v(28.57, 135.97) * mm});
            skArc(sketch, "E39.filletArc", {"start": v(34.93, 135.97) * mm, "mid": v(30.43, 134.1) * mm, "end": v(28.58, 129.62) * mm});
            skPoint(sketch, "E40.visualSharp", {"position": v(98.43, 135.97) * mm});
            skArc(sketch, "E40.filletArc", {"start": v(98.43, 129.62) * mm, "mid": v(96.57, 134.1) * mm, "end": v(92.08, 135.97) * mm});
            skPoint(sketch, "E41.visualSharp", {"position": v(98.43, 24.2) * mm});
            skArc(sketch, "E41.filletArc", {"start": v(92.08, 24.2) * mm, "mid": v(96.57, 26.07) * mm, "end": v(98.43, 30.56) * mm});
            skPoint(sketch, "E42.visualSharp", {"position": v(28.58, 24.2) * mm});
            skArc(sketch, "E42.filletArc", {"start": v(28.58, 30.56) * mm, "mid": v(30.43, 26.07) * mm, "end": v(34.93, 24.2) * mm});
            skSolve(sketch);
        }
        {
            var Q0;
            Q0=makeQuery(id+"F4.imprint","IMPRINT",FACE,{"disambiguationData":[TD([[makeQuery(id+"F4.imprint","IMPRINT",EDGE,{"derivedFrom":sQuery(id+"F4.wireOp",EDGE,"E38.right")}),1.0]])]});
            var Q1;
            Q1=makeQuery(id+"F4.imprint","IMPRINT",FACE,{"disambiguationData":[TD([[makeQuery(id+"F4.imprint","IMPRINT",EDGE,{"derivedFrom":sQuery(id+"F4.wireOp",EDGE,"E38.left")}),-1.0]])]});
            extrude(context, id + "F5", {"entities" : qUnion([Q0, Q1]), "operationType" : NewBodyOperationType.REMOVE, "oppositeDirection" : true, "depth" : 127 * mm, "hasSecondDirection" : true, "secondDirectionOppositeDirection" : true, "secondDirectionDepth" : 2.54 * mm});
        }
        {
            var Q0;
            Q0=makeQuery(id+"F1.opExtrude","CAP_FACE",FACE,{"disambiguationData":[OSD([sQuery(id+"F0.wireOp",EDGE,"E0.bottom"),sQuery(id+"F0.wireOp",EDGE,"E0.top"),sQuery(id+"F0.wireOp",EDGE,"E0.left"),sQuery(id+"F0.wireOp",EDGE,"E0.right"),sQuery(id+"F0.wireOp",EDGE,"E4"),sQuery(id+"F0.wireOp",EDGE,"E5.MirrorC"),sQuery(id+"F0.wireOp",EDGE,"E6.MirrorC"),sQuery(id+"F0.wireOp",EDGE,"E7.MirrorC"),sQuery(id+"F0.wireOp",EDGE,"E8"),sQuery(id+"F0.wireOp",EDGE,"E9.MirrorC"),sQuery(id+"F0.wireOp",EDGE,"E10.filletArc"),sQuery(id+"F0.wireOp",EDGE,"E11.filletArc"),sQuery(id+"F0.wireOp",EDGE,"E12.filletArc"),sQuery(id+"F0.wireOp",EDGE,"E13.filletArc")])],"isStart":false});
            var sketch = newSketch(context, id + "F6", { "sketchPlane" : qUnion([Q0])});
            skPoint(sketch, "E43", {"position": v(63.5, 149.29) * mm});
            skLineSegment(sketch, "E44", {"start": v(53.97, 158.75) * mm, "end": v(53.97, 148.6) * mm});
            skLineSegment(sketch, "E45", {"start": v(73.02, 148.6) * mm, "end": v(73.02, 158.75) * mm});
            skArc(sketch, "E46", {"start": v(53.97, 148.6) * mm, "mid": v(63.5, 139.07) * mm, "end": v(73.02, 148.6) * mm});
            skLineSegment(sketch, "E47", {"start": v(63.5, 158.75) * mm, "end": v(63.5, 0) * mm});
            skPoint(sketch, "E48", {"position": v(63.5, 79.38) * mm});
            skLineSegment(sketch, "E49", {"start": v(63.5, 79.38) * mm, "end": v(89.75, 79.38) * mm});
            skArc(sketch, "E50.MirrorCS", {"start": v(53.97, 10.16) * mm, "mid": v(63.5, 19.69) * mm, "end": v(73.02, 10.16) * mm});
            skLineSegment(sketch, "E51.MirrorCS", {"start": v(53.97, 0) * mm, "end": v(53.97, 10.16) * mm});
            skLineSegment(sketch, "E52.MirrorCS", {"start": v(73.02, 10.16) * mm, "end": v(73.02, 0) * mm});
            skSolve(sketch);
        }
        {
            var Q0;
            Q0 = qSketchRegion(id + "F6", true);
            var Q1;
            {var subQ5=sQuery(id+"F6.wireOp",EDGE,"E44");Q1=makeQuery(id+"F6.imprint","IMPRINT",FACE,{"disambiguationData":[TD([[makeQuery(id+"F6.imprint","IMPRINT",EDGE,{"derivedFrom":subQ5}),1.0]])]});}
            var Q2;
            {var subQ8=sQuery(id+"F6.wireOp",EDGE,"E45");Q2=makeQuery(id+"F6.imprint","IMPRINT",FACE,{"disambiguationData":[TD([[makeQuery(id+"F6.imprint","IMPRINT",EDGE,{"derivedFrom":subQ8}),1.0]])]});}
            var Q3;
            {var subQ0=sQuery(id+"F6.wireOp",EDGE,"E52.MirrorCS");Q3=makeQuery(id+"F6.imprint","IMPRINT",FACE,{"disambiguationData":[TD([[makeQuery(id+"F6.imprint","IMPRINT",EDGE,{"derivedFrom":subQ0}),-1.0]])]});}
            var Q4;
            {var subQ0=sQuery(id+"F6.wireOp",EDGE,"E51.MirrorCS");Q4=makeQuery(id+"F6.imprint","IMPRINT",FACE,{"disambiguationData":[TD([[makeQuery(id+"F6.imprint","IMPRINT",EDGE,{"derivedFrom":subQ0}),-1.0]])]});}
            extrude(context, id + "F7", {"entities" : qUnion([Q0, Q1, Q2, Q3, Q4]), "operationType" : NewBodyOperationType.REMOVE, "oppositeDirection" : true, "depth" : 124.46 * mm});
        }
        {
            var Q0;
            Q0=makeQuery(id+"F1.opExtrude","CAP_FACE",FACE,{"disambiguationData":[OSD([sQuery(id+"F0.wireOp",EDGE,"E0.bottom"),sQuery(id+"F0.wireOp",EDGE,"E0.top"),sQuery(id+"F0.wireOp",EDGE,"E0.left"),sQuery(id+"F0.wireOp",EDGE,"E0.right"),sQuery(id+"F0.wireOp",EDGE,"E4"),sQuery(id+"F0.wireOp",EDGE,"E5.MirrorC"),sQuery(id+"F0.wireOp",EDGE,"E6.MirrorC"),sQuery(id+"F0.wireOp",EDGE,"E7.MirrorC"),sQuery(id+"F0.wireOp",EDGE,"E8"),sQuery(id+"F0.wireOp",EDGE,"E9.MirrorC"),sQuery(id+"F0.wireOp",EDGE,"E10.filletArc"),sQuery(id+"F0.wireOp",EDGE,"E11.filletArc"),sQuery(id+"F0.wireOp",EDGE,"E12.filletArc"),sQuery(id+"F0.wireOp",EDGE,"E13.filletArc")])],"isStart":true});
            var sketch = newSketch(context, id + "F8", { "sketchPlane" : qUnion([Q0])});
            skLineSegment(sketch, "E53", {"start": v(63.5, 0) * mm, "end": v(63.5, -24.2) * mm});
            skLineSegment(sketch, "E54", {"start": v(96.57, -26.07) * mm, "end": v(119.56, -7.44) * mm});
            skLineSegment(sketch, "E55", {"start": v(63.5, -21.67) * mm, "end": v(102, -21.67) * mm});
            skLineSegment(sketch, "E56", {"start": v(73.6, 0) * mm, "end": v(73.6, -21.67) * mm});
            skLineSegment(sketch, "E57", {"start": v(72, -21.67) * mm, "end": v(72, 0) * mm});
            skLineSegment(sketch, "E58.1.0.0", {"start": v(75.18, -21.67) * mm, "end": v(75.18, 0) * mm});
            skLineSegment(sketch, "E58.1.0.1", {"start": v(76.77, 0) * mm, "end": v(76.77, -21.67) * mm});
            skLineSegment(sketch, "E58.2.0.0", {"start": v(78.36, -21.67) * mm, "end": v(78.36, 0) * mm});
            skLineSegment(sketch, "E58.2.0.1", {"start": v(79.95, 0) * mm, "end": v(79.95, -21.67) * mm});
            skLineSegment(sketch, "E58.3.0.0", {"start": v(81.53, -21.67) * mm, "end": v(81.53, 0) * mm});
            skLineSegment(sketch, "E58.3.0.1", {"start": v(83.12, 0) * mm, "end": v(83.12, -21.67) * mm});
            skLineSegment(sketch, "E58.4.0.0", {"start": v(84.7, -21.67) * mm, "end": v(84.7, 0) * mm});
            skLineSegment(sketch, "E58.4.0.1", {"start": v(86.3, 0) * mm, "end": v(86.3, -21.67) * mm});
            skLineSegment(sketch, "E58.5.0.0", {"start": v(87.88, -21.67) * mm, "end": v(87.88, 0) * mm});
            skLineSegment(sketch, "E58.5.0.1", {"start": v(89.47, 0) * mm, "end": v(89.47, -21.67) * mm});
            skLineSegment(sketch, "E58.direction1", {"start": v(72, -21.67) * mm, "end": v(75.18, -21.67) * mm, "construction": true});
            skLineSegment(sketch, "E59.MirrorCS", {"start": v(40.7, 0) * mm, "end": v(40.7, -21.67) * mm});
            skLineSegment(sketch, "E60.MirrorCS", {"start": v(42.3, -21.67) * mm, "end": v(42.3, 0) * mm});
            skLineSegment(sketch, "E61.MirrorCS", {"start": v(43.88, 0) * mm, "end": v(43.88, -21.67) * mm});
            skLineSegment(sketch, "E62.MirrorCS", {"start": v(45.47, -21.67) * mm, "end": v(45.47, 0) * mm});
            skLineSegment(sketch, "E63.MirrorCS", {"start": v(51.82, -21.67) * mm, "end": v(51.82, 0) * mm});
            skLineSegment(sketch, "E64.MirrorCS", {"start": v(47.05, 0) * mm, "end": v(47.05, -21.67) * mm});
            skLineSegment(sketch, "E65.MirrorCS", {"start": v(48.64, -21.67) * mm, "end": v(48.64, 0) * mm});
            skLineSegment(sketch, "E66.MirrorCS", {"start": v(55, -21.67) * mm, "end": v(55, 0) * mm});
            skLineSegment(sketch, "E67.MirrorCS", {"start": v(37.53, 0) * mm, "end": v(37.53, -21.67) * mm});
            skLineSegment(sketch, "E68.MirrorCS", {"start": v(39.12, -21.67) * mm, "end": v(39.12, 0) * mm});
            skLineSegment(sketch, "E69.MirrorCS", {"start": v(50.23, 0) * mm, "end": v(50.23, -21.67) * mm});
            skLineSegment(sketch, "E70.MirrorCS", {"start": v(63.5, -21.67) * mm, "end": v(25, -21.67) * mm});
            skLineSegment(sketch, "E71.MirrorCS", {"start": v(53.4, 0) * mm, "end": v(53.4, -21.67) * mm});
            skLineSegment(sketch, "E72", {"start": v(0, -79.38) * mm, "end": v(127, -79.38) * mm, "construction": true});
            skLineSegment(sketch, "E73.MirrorCS", {"start": v(87.88, -137.08) * mm, "end": v(87.88, -158.75) * mm});
            skLineSegment(sketch, "E74.MirrorCS", {"start": v(89.47, -158.75) * mm, "end": v(89.47, -137.08) * mm});
            skLineSegment(sketch, "E75.MirrorCS", {"start": v(73.6, -158.75) * mm, "end": v(73.6, -137.08) * mm});
            skLineSegment(sketch, "E76.MirrorCS", {"start": v(72, -137.08) * mm, "end": v(72, -158.75) * mm});
            skLineSegment(sketch, "E77.MirrorCS", {"start": v(75.18, -137.08) * mm, "end": v(75.18, -158.75) * mm});
            skLineSegment(sketch, "E78.MirrorCS", {"start": v(76.77, -158.75) * mm, "end": v(76.77, -137.08) * mm});
            skLineSegment(sketch, "E79.MirrorCS", {"start": v(78.36, -137.08) * mm, "end": v(78.36, -158.75) * mm});
            skLineSegment(sketch, "E80.MirrorCS", {"start": v(79.95, -158.75) * mm, "end": v(79.95, -137.08) * mm});
            skLineSegment(sketch, "E81.MirrorCS", {"start": v(81.53, -137.08) * mm, "end": v(81.53, -158.75) * mm});
            skLineSegment(sketch, "E82.MirrorCS", {"start": v(83.12, -158.75) * mm, "end": v(83.12, -137.08) * mm});
            skLineSegment(sketch, "E83.MirrorCS", {"start": v(84.7, -137.08) * mm, "end": v(84.7, -158.75) * mm});
            skLineSegment(sketch, "E84.MirrorCS", {"start": v(86.3, -158.75) * mm, "end": v(86.3, -137.08) * mm});
            skLineSegment(sketch, "E85.MirrorCS", {"start": v(37.53, -158.75) * mm, "end": v(37.53, -137.08) * mm});
            skLineSegment(sketch, "E86.MirrorCS", {"start": v(43.88, -158.75) * mm, "end": v(43.88, -137.08) * mm});
            skLineSegment(sketch, "E87.MirrorCS", {"start": v(39.12, -137.08) * mm, "end": v(39.12, -158.75) * mm});
            skLineSegment(sketch, "E88.MirrorCS", {"start": v(40.7, -158.75) * mm, "end": v(40.7, -137.08) * mm});
            skLineSegment(sketch, "E89.MirrorCS", {"start": v(48.64, -137.08) * mm, "end": v(48.64, -158.75) * mm});
            skLineSegment(sketch, "E90.MirrorCS", {"start": v(42.3, -137.08) * mm, "end": v(42.3, -158.75) * mm});
            skLineSegment(sketch, "E91.MirrorCS", {"start": v(47.05, -158.75) * mm, "end": v(47.05, -137.08) * mm});
            skLineSegment(sketch, "E92.MirrorCS", {"start": v(55, -137.08) * mm, "end": v(55, -158.75) * mm});
            skLineSegment(sketch, "E93.MirrorCS", {"start": v(50.23, -158.75) * mm, "end": v(50.23, -137.08) * mm});
            skLineSegment(sketch, "E94.MirrorCS", {"start": v(45.47, -137.08) * mm, "end": v(45.47, -158.75) * mm});
            skLineSegment(sketch, "E95.MirrorCS", {"start": v(51.82, -137.08) * mm, "end": v(51.82, -158.75) * mm});
            skLineSegment(sketch, "E96.MirrorCS", {"start": v(53.4, -158.75) * mm, "end": v(53.4, -137.08) * mm});
            skLineSegment(sketch, "E97.MirrorCS", {"start": v(63.5, -137.08) * mm, "end": v(102, -137.08) * mm});
            skLineSegment(sketch, "E98.MirrorCS", {"start": v(63.5, -137.08) * mm, "end": v(25, -137.08) * mm});
            skSolve(sketch);
        }
        {
            var Q0;
            Q0 = qSketchRegion(id + "F8", true);
            var Q1;
            {var subQ0=sQuery(id+"F8.wireOp",EDGE,"E63.MirrorCS");Q1=makeQuery(id+"F8.imprint","IMPRINT",FACE,{"disambiguationData":[TD([[makeQuery(id+"F8.imprint","IMPRINT",EDGE,{"derivedFrom":subQ0}),1.0]])]});}
            var Q2;
            {var subQ0=sQuery(id+"F8.wireOp",EDGE,"E64.MirrorCS");Q2=makeQuery(id+"F8.imprint","IMPRINT",FACE,{"disambiguationData":[TD([[makeQuery(id+"F8.imprint","IMPRINT",EDGE,{"derivedFrom":subQ0}),1.0]])]});}
            var Q3;
            {var subQ0=sQuery(id+"F8.wireOp",EDGE,"E61.MirrorCS");Q3=makeQuery(id+"F8.imprint","IMPRINT",FACE,{"disambiguationData":[TD([[makeQuery(id+"F8.imprint","IMPRINT",EDGE,{"derivedFrom":subQ0}),1.0]])]});}
            var Q4;
            {var subQ0=sQuery(id+"F8.wireOp",EDGE,"E59.MirrorCS");Q4=makeQuery(id+"F8.imprint","IMPRINT",FACE,{"disambiguationData":[TD([[makeQuery(id+"F8.imprint","IMPRINT",EDGE,{"derivedFrom":subQ0}),1.0]])]});}
            var Q5;
            {var subQ0=sQuery(id+"F8.wireOp",EDGE,"E67.MirrorCS");Q5=makeQuery(id+"F8.imprint","IMPRINT",FACE,{"disambiguationData":[TD([[makeQuery(id+"F8.imprint","IMPRINT",EDGE,{"derivedFrom":subQ0}),1.0]])]});}
            var Q6;
            {var subQ0=sQuery(id+"F8.wireOp",EDGE,"E58.1.0.0");Q6=makeQuery(id+"F8.imprint","IMPRINT",FACE,{"disambiguationData":[TD([[makeQuery(id+"F8.imprint","IMPRINT",EDGE,{"derivedFrom":subQ0}),-1.0]])]});}
            var Q7;
            {var subQ0=sQuery(id+"F8.wireOp",EDGE,"E58.2.0.0");Q7=makeQuery(id+"F8.imprint","IMPRINT",FACE,{"disambiguationData":[TD([[makeQuery(id+"F8.imprint","IMPRINT",EDGE,{"derivedFrom":subQ0}),-1.0]])]});}
            var Q8;
            {var subQ0=sQuery(id+"F8.wireOp",EDGE,"E58.3.0.0");Q8=makeQuery(id+"F8.imprint","IMPRINT",FACE,{"disambiguationData":[TD([[makeQuery(id+"F8.imprint","IMPRINT",EDGE,{"derivedFrom":subQ0}),-1.0]])]});}
            var Q9;
            {var subQ0=sQuery(id+"F8.wireOp",EDGE,"E58.4.0.0");Q9=makeQuery(id+"F8.imprint","IMPRINT",FACE,{"disambiguationData":[TD([[makeQuery(id+"F8.imprint","IMPRINT",EDGE,{"derivedFrom":subQ0}),-1.0]])]});}
            var Q10;
            {var subQ0=sQuery(id+"F8.wireOp",EDGE,"E58.5.0.0");Q10=makeQuery(id+"F8.imprint","IMPRINT",FACE,{"disambiguationData":[TD([[makeQuery(id+"F8.imprint","IMPRINT",EDGE,{"derivedFrom":subQ0}),-1.0]])]});}
            var Q11;
            {var subQ0=sQuery(id+"F8.wireOp",EDGE,"E85.MirrorCS");Q11=makeQuery(id+"F8.imprint","IMPRINT",FACE,{"disambiguationData":[TD([[makeQuery(id+"F8.imprint","IMPRINT",EDGE,{"derivedFrom":subQ0}),-1.0]])]});}
            var Q12;
            {var subQ0=sQuery(id+"F8.wireOp",EDGE,"E88.MirrorCS");Q12=makeQuery(id+"F8.imprint","IMPRINT",FACE,{"disambiguationData":[TD([[makeQuery(id+"F8.imprint","IMPRINT",EDGE,{"derivedFrom":subQ0}),-1.0]])]});}
            var Q13;
            {var subQ0=sQuery(id+"F8.wireOp",EDGE,"E86.MirrorCS");Q13=makeQuery(id+"F8.imprint","IMPRINT",FACE,{"disambiguationData":[TD([[makeQuery(id+"F8.imprint","IMPRINT",EDGE,{"derivedFrom":subQ0}),-1.0]])]});}
            var Q14;
            {var subQ0=sQuery(id+"F8.wireOp",EDGE,"E89.MirrorCS");Q14=makeQuery(id+"F8.imprint","IMPRINT",FACE,{"disambiguationData":[TD([[makeQuery(id+"F8.imprint","IMPRINT",EDGE,{"derivedFrom":subQ0}),-1.0]])]});}
            var Q15;
            {var subQ0=sQuery(id+"F8.wireOp",EDGE,"E93.MirrorCS");Q15=makeQuery(id+"F8.imprint","IMPRINT",FACE,{"disambiguationData":[TD([[makeQuery(id+"F8.imprint","IMPRINT",EDGE,{"derivedFrom":subQ0}),-1.0]])]});}
            var Q16;
            {var subQ0=sQuery(id+"F8.wireOp",EDGE,"E77.MirrorCS");Q16=makeQuery(id+"F8.imprint","IMPRINT",FACE,{"disambiguationData":[TD([[makeQuery(id+"F8.imprint","IMPRINT",EDGE,{"derivedFrom":subQ0}),1.0]])]});}
            var Q17;
            {var subQ0=sQuery(id+"F8.wireOp",EDGE,"E79.MirrorCS");Q17=makeQuery(id+"F8.imprint","IMPRINT",FACE,{"disambiguationData":[TD([[makeQuery(id+"F8.imprint","IMPRINT",EDGE,{"derivedFrom":subQ0}),1.0]])]});}
            var Q18;
            {var subQ0=sQuery(id+"F8.wireOp",EDGE,"E81.MirrorCS");Q18=makeQuery(id+"F8.imprint","IMPRINT",FACE,{"disambiguationData":[TD([[makeQuery(id+"F8.imprint","IMPRINT",EDGE,{"derivedFrom":subQ0}),1.0]])]});}
            var Q19;
            {var subQ0=sQuery(id+"F8.wireOp",EDGE,"E83.MirrorCS");Q19=makeQuery(id+"F8.imprint","IMPRINT",FACE,{"disambiguationData":[TD([[makeQuery(id+"F8.imprint","IMPRINT",EDGE,{"derivedFrom":subQ0}),1.0]])]});}
            var Q20;
            {var subQ0=sQuery(id+"F8.wireOp",EDGE,"E73.MirrorCS");Q20=makeQuery(id+"F8.imprint","IMPRINT",FACE,{"disambiguationData":[TD([[makeQuery(id+"F8.imprint","IMPRINT",EDGE,{"derivedFrom":subQ0}),1.0]])]});}
            extrude(context, id + "F9", {"entities" : qUnion([Q0, Q1, Q2, Q3, Q4, Q5, Q6, Q7, Q8, Q9, Q10, Q11, Q12, Q13, Q14, Q15, Q16, Q17, Q18, Q19, Q20]), "operationType" : NewBodyOperationType.REMOVE, "oppositeDirection" : true, "depth" : 127 * mm, "hasSecondDirection" : true, "secondDirectionOppositeDirection" : true, "secondDirectionDepth" : 2.54 * mm});
        }
        {
            var Q0;
            Q0=makeQuery(id+"F1.opExtrude","CAP_FACE",FACE,{"disambiguationData":[OSD([sQuery(id+"F0.wireOp",EDGE,"E0.bottom"),sQuery(id+"F0.wireOp",EDGE,"E0.top"),sQuery(id+"F0.wireOp",EDGE,"E0.left"),sQuery(id+"F0.wireOp",EDGE,"E0.right"),sQuery(id+"F0.wireOp",EDGE,"E4"),sQuery(id+"F0.wireOp",EDGE,"E5.MirrorC"),sQuery(id+"F0.wireOp",EDGE,"E6.MirrorC"),sQuery(id+"F0.wireOp",EDGE,"E7.MirrorC"),sQuery(id+"F0.wireOp",EDGE,"E8"),sQuery(id+"F0.wireOp",EDGE,"E9.MirrorC"),sQuery(id+"F0.wireOp",EDGE,"E10.filletArc"),sQuery(id+"F0.wireOp",EDGE,"E11.filletArc"),sQuery(id+"F0.wireOp",EDGE,"E12.filletArc"),sQuery(id+"F0.wireOp",EDGE,"E13.filletArc")])],"isStart":false});
            var sketch = newSketch(context, id + "F10", { "sketchPlane" : qUnion([Q0])});
            skArc(sketch, "E99", {"start": v(0, 125.8) * mm, "mid": v(24.74, 134.88) * mm, "end": v(35.94, 158.75) * mm});
            skArc(sketch, "E100.MirrorCS", {"start": v(127, 125.8) * mm, "mid": v(102.26, 134.88) * mm, "end": v(91.06, 158.75) * mm});
            skArc(sketch, "E101.MirrorCS", {"start": v(0, 32.96) * mm, "mid": v(24.74, 23.87) * mm, "end": v(35.94, 0) * mm});
            skArc(sketch, "E102.MirrorCS", {"start": v(127, 32.96) * mm, "mid": v(102.26, 23.87) * mm, "end": v(91.06, 0) * mm});
            skSolve(sketch);
        }
        {
            var Q0;
            Q0 = qSketchRegion(id + "F10", true);
            var Q1;
            {var subQ0=sQuery(id+"F10.wireOp",EDGE,"E99");Q1=makeQuery(id+"F10.imprint","IMPRINT",FACE,{"disambiguationData":[TD([[makeQuery(id+"F10.imprint","IMPRINT",EDGE,{"derivedFrom":subQ0}),1.0]])]});}
            var Q2;
            {var subQ0=sQuery(id+"F10.wireOp",EDGE,"E100.MirrorCS");Q2=makeQuery(id+"F10.imprint","IMPRINT",FACE,{"disambiguationData":[TD([[makeQuery(id+"F10.imprint","IMPRINT",EDGE,{"derivedFrom":subQ0}),-1.0]])]});}
            var Q3;
            {var subQ0=sQuery(id+"F10.wireOp",EDGE,"E102.MirrorCS");Q3=makeQuery(id+"F10.imprint","IMPRINT",FACE,{"disambiguationData":[TD([[makeQuery(id+"F10.imprint","IMPRINT",EDGE,{"derivedFrom":subQ0}),1.0]])]});}
            var Q4;
            {var subQ0=sQuery(id+"F10.wireOp",EDGE,"E101.MirrorCS");Q4=makeQuery(id+"F10.imprint","IMPRINT",FACE,{"disambiguationData":[TD([[makeQuery(id+"F10.imprint","IMPRINT",EDGE,{"derivedFrom":subQ0}),-1.0]])]});}
            extrude(context, id + "F11", {"entities" : qUnion([Q0, Q1, Q2, Q3, Q4]), "operationType" : NewBodyOperationType.REMOVE, "oppositeDirection" : true, "depth" : 124.46 * mm});
        }
    });
